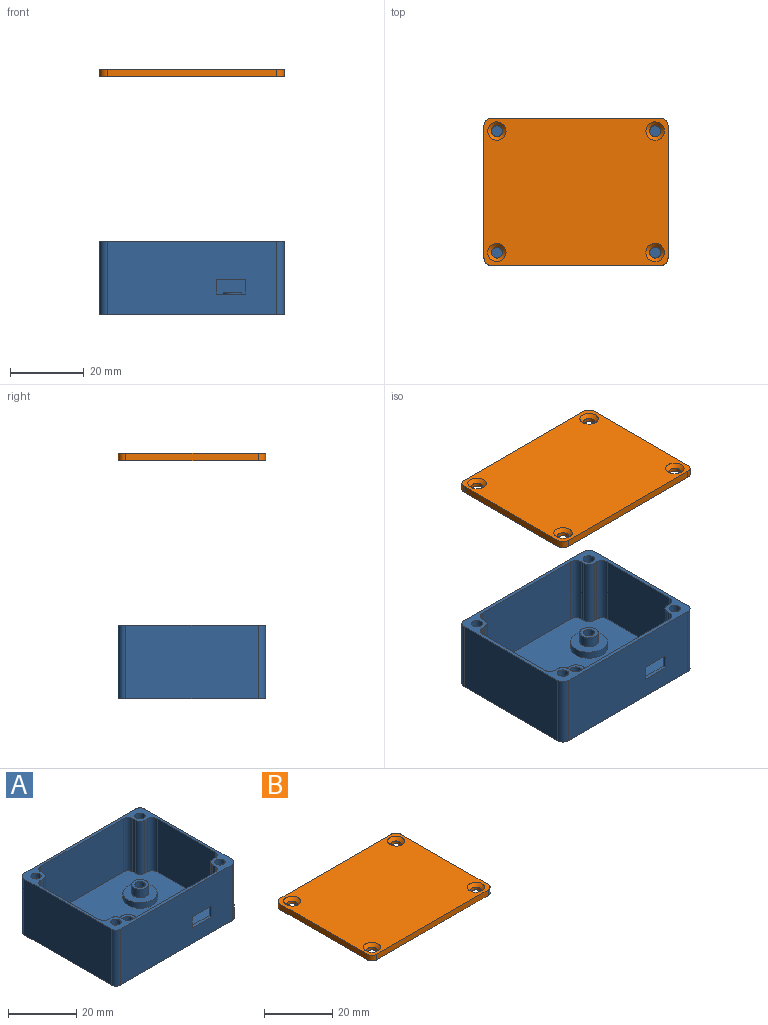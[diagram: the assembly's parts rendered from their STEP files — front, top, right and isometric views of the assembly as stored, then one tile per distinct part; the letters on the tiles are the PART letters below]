
ASSEMBLY  parts=2 mates=1
PART A: 71 faces, bbox 50x40x20 mm
  f0: plane 34x19mm, normal (0,1,0), area 614mm2, adj f5,f9,f51,f55,f67,f68,f69,f70
  f1: plane 46x20mm, normal (0,-1,0), area 888mm2, adj f2,f9,f64,f65,f67,f68,f69,f70
  f2: plane 50x40mm, normal (0,0,-1), area 1949.8mm2, adj f1,f10,f11,f12,f37,f38,f39,f40
  f3: cylinder r=1.5mm len=4mm, axis (0,0,-1), area 37.7mm2, adj f30,f50
  f4: cylinder r=1.5mm len=4mm, axis (0,0,-1), area 37.7mm2, adj f32,f43
  f5: plane 48x38mm, normal (0,0,1), area 1563.5mm2, adj f0,f6,f7,f8,f13,f14,f15,f16
  f6: plane 24x19mm, normal (-1,0,0), area 456mm2, adj f5,f9,f53,f57
  f7: plane 24x19mm, normal (1,0,0), area 456mm2, adj f5,f9,f56,f62
  f8: plane 34x19mm, normal (0,-1,0), area 646mm2, adj f5,f9,f58,f60
  f9: plane 50x40mm, normal (0,0,1), area 247.7mm2, adj f0,f1,f6,f7,f8,f10,f11,f12
  f10: plane 46x20mm, normal (0,1,0), area 920mm2, adj f2,f9,f63,f66
  f11: plane 36x20mm, normal (-1,0,0), area 720mm2, adj f2,f9,f63,f64
  f12: plane 36x20mm, normal (1,0,0), area 720mm2, adj f2,f9,f65,f66
  f13: plane 19x1mm, normal (0,-1,0), area 19mm2, adj f5,f9,f61,f62
  f14: plane 19x1mm, normal (1,0,0), area 19mm2, adj f5,f9,f60,f61
  f15: plane 19x1mm, normal (0,-1,0), area 19mm2, adj f5,f9,f57,f59
  f16: plane 19x1mm, normal (-1,0,0), area 19mm2, adj f5,f9,f58,f59
  f17: plane 19x1mm, normal (0,1,0), area 19mm2, adj f5,f9,f54,f56
  f18: plane 19x1mm, normal (1,0,0), area 19mm2, adj f5,f9,f54,f55
  f19: plane 19x1mm, normal (0,1,0), area 19mm2, adj f5,f9,f52,f53
  f20: plane 19x1mm, normal (-1,0,0), area 19mm2, adj f5,f9,f51,f52
  f21: cylinder r=1.5mm len=10mm, axis (0,0,1), area 94.2mm2, adj f9,f22
  f22: plane 3x3mm, normal (0,0,1), area 7.1mm2, adj f21
  f23: cylinder r=1.5mm len=10mm, axis (0,0,1), area 94.2mm2, adj f9,f24
  f24: plane 3x3mm, normal (0,0,1), area 7.1mm2, adj f23
  f25: cylinder r=1.5mm len=10mm, axis (0,0,1), area 94.2mm2, adj f9,f26
  f26: plane 3x3mm, normal (0,0,1), area 7.1mm2, adj f25
  f27: cylinder r=1.5mm len=10mm, axis (0,0,1), area 94.2mm2, adj f9,f28
  f28: plane 3x3mm, normal (0,0,1), area 7.1mm2, adj f27
  f29: cylinder r=2.5mm len=5mm, axis (0,0,-1), area 47.1mm2, adj f30,f34
  f30: plane 5x5mm, normal (0,0,1), area 12.6mm2, adj f3,f29
  f31: cylinder r=2.5mm len=5mm, axis (0,0,-1), area 47.1mm2, adj f32,f36
  f32: plane 5x5mm, normal (0,0,1), area 12.6mm2, adj f4,f31
  f33: cylinder r=5mm len=10mm, axis (0,0,-1), area 62.8mm2, adj f5,f34
  f34: plane 10x10mm, normal (0,0,1), area 58.9mm2, adj f29,f33
  f35: cylinder r=5mm len=10mm, axis (0,0,-1), area 62.8mm2, adj f5,f36
  f36: plane 10x10mm, normal (0,0,1), area 58.9mm2, adj f31,f35
  f37: plane 2.98x2mm, normal (0.12,-0.99,0), area 6mm2, adj f2,f38,f42,f43
  f38: plane 2.4x2mm, normal (-0.8,-0.6,0), area 6mm2, adj f2,f37,f39,f43
  f39: plane 2.76x2mm, normal (-0.92,0.39,0), area 6mm2, adj f2,f38,f40,f43
  f40: plane 2.98x2mm, normal (-0.12,0.99,0), area 6mm2, adj f2,f39,f41,f43
  f41: plane 2.4x2mm, normal (0.8,0.6,0), area 6mm2, adj f2,f40,f42,f43
  f42: plane 2.76x2mm, normal (0.92,-0.39,0), area 6mm2, adj f2,f37,f41,f43
  f43: plane 5.96x5.52mm, normal (0,0,-1), area 16.3mm2, adj f4,f37,f38,f39,f40,f41,f42
  f44: plane 2.95x2mm, normal (0.18,-0.98,0), area 6mm2, adj f2,f45,f49,f50
  f45: plane 2.28x2mm, normal (-0.76,-0.65,0), area 6mm2, adj f2,f44,f46,f50
  f46: plane 2.83x2mm, normal (-0.94,0.33,0), area 6mm2, adj f2,f45,f47,f50
  f47: plane 2.95x2mm, normal (-0.18,0.98,0), area 6mm2, adj f2,f46,f48,f50
  f48: plane 2.28x2mm, normal (0.76,0.65,0), area 6mm2, adj f2,f47,f49,f50
  f49: plane 2.83x2mm, normal (0.94,-0.33,0), area 6mm2, adj f2,f44,f48,f50
  f50: plane 5.9x5.66mm, normal (0,0,-1), area 16.3mm2, adj f3,f44,f45,f46,f47,f48,f49
  f51: cylinder r=2mm len=19mm, axis (0,0,1), area 59.7mm2, adj f0,f5,f9,f20
  f52: cylinder r=2mm len=19mm, axis (0,0,1), area 59.7mm2, adj f5,f9,f19,f20
  f53: cylinder r=2mm len=19mm, axis (0,0,1), area 59.7mm2, adj f5,f6,f9,f19
  f54: cylinder r=2mm len=19mm, axis (0,0,1), area 59.7mm2, adj f5,f9,f17,f18
  f55: cylinder r=2mm len=19mm, axis (0,0,-1), area 59.7mm2, adj f0,f5,f9,f18
  f56: cylinder r=2mm len=19mm, axis (0,0,1), area 59.7mm2, adj f5,f7,f9,f17
  f57: cylinder r=2mm len=19mm, axis (0,0,-1), area 59.7mm2, adj f5,f6,f9,f15
  f58: cylinder r=2mm len=19mm, axis (0,0,1), area 59.7mm2, adj f5,f8,f9,f16
  f59: cylinder r=2mm len=19mm, axis (0,0,1), area 59.7mm2, adj f5,f9,f15,f16
  f60: cylinder r=2mm len=19mm, axis (0,0,-1), area 59.7mm2, adj f5,f8,f9,f14
  f61: cylinder r=2mm len=19mm, axis (0,0,1), area 59.7mm2, adj f5,f9,f13,f14
  f62: cylinder r=2mm len=19mm, axis (0,0,-1), area 59.7mm2, adj f5,f7,f9,f13
  f63: cylinder r=2mm len=20mm, axis (0,0,1), area 62.8mm2, adj f2,f9,f10,f11
  f64: cylinder r=2mm len=20mm, axis (0,0,-1), area 62.8mm2, adj f1,f2,f9,f11
  f65: cylinder r=2mm len=20mm, axis (0,0,1), area 62.8mm2, adj f1,f2,f9,f12
  f66: cylinder r=2mm len=20mm, axis (0,0,-1), area 62.8mm2, adj f2,f9,f10,f12
  f67: plane 8x1mm, normal (0,0,-1), area 8mm2, adj f0,f1,f68,f70
  f68: plane 4x1mm, normal (1,0,0), area 4mm2, adj f0,f1,f67,f69
  f69: plane 8x1mm, normal (0,0,1), area 8mm2, adj f0,f1,f68,f70
  f70: plane 4x1mm, normal (-1,0,0), area 4mm2, adj f0,f1,f67,f69
PART B: 18 faces, bbox 50x40x2 mm
  f0: plane 46x2mm, normal (0,1,0), area 92mm2, adj f4,f5,f14,f17
  f1: plane 36x2mm, normal (-1,0,0), area 72mm2, adj f4,f5,f14,f15
  f2: plane 46x2mm, normal (0,-1,0), area 92mm2, adj f4,f5,f15,f16
  f3: plane 36x2mm, normal (1,0,0), area 72mm2, adj f4,f5,f16,f17
  f4: plane 50x40mm, normal (0,0,1), area 1918mm2, adj f0,f1,f2,f3,f10,f11,f12,f13
  f5: plane 50x40mm, normal (0,0,-1), area 1968.3mm2, adj f0,f1,f2,f3,f6,f7,f8,f9
  f6: cylinder r=1.5mm len=3mm, axis (0,0,1), area 9.4mm2, adj f5,f10
  f7: cylinder r=1.5mm len=3mm, axis (0,0,1), area 9.4mm2, adj f5,f13
  f8: cylinder r=1.5mm len=3mm, axis (0,0,1), area 9.4mm2, adj f5,f12
  f9: cylinder r=1.5mm len=3mm, axis (0,0,1), area 9.4mm2, adj f5,f11
  f10: cone r=1.5mm half-angle=45deg, axis (0,0,1), area 17.8mm2, adj f4,f6
  f11: cone r=1.5mm half-angle=45deg, axis (0,0,1), area 17.8mm2, adj f4,f9
  f12: cone r=1.5mm half-angle=45deg, axis (0,0,1), area 17.8mm2, adj f4,f8
  f13: cone r=1.5mm half-angle=45deg, axis (0,0,1), area 17.8mm2, adj f4,f7
  f14: cylinder r=2mm len=2mm, axis (0,0,1), area 6.3mm2, adj f0,f1,f4,f5
  f15: cylinder r=2mm len=2mm, axis (0,0,-1), area 6.3mm2, adj f1,f2,f4,f5
  f16: cylinder r=2mm len=2mm, axis (0,0,1), area 6.3mm2, adj f2,f3,f4,f5
  f17: cylinder r=2mm len=2mm, axis (0,0,-1), area 6.3mm2, adj f0,f3,f4,f5
PLACE A at identity fixed
PLACE B t=(-72.26,-1.95,64.65)mm
MATE slider A.f25 <-> B.f9  axis (0,0,1) through (-17.8,14.1,20)mm
